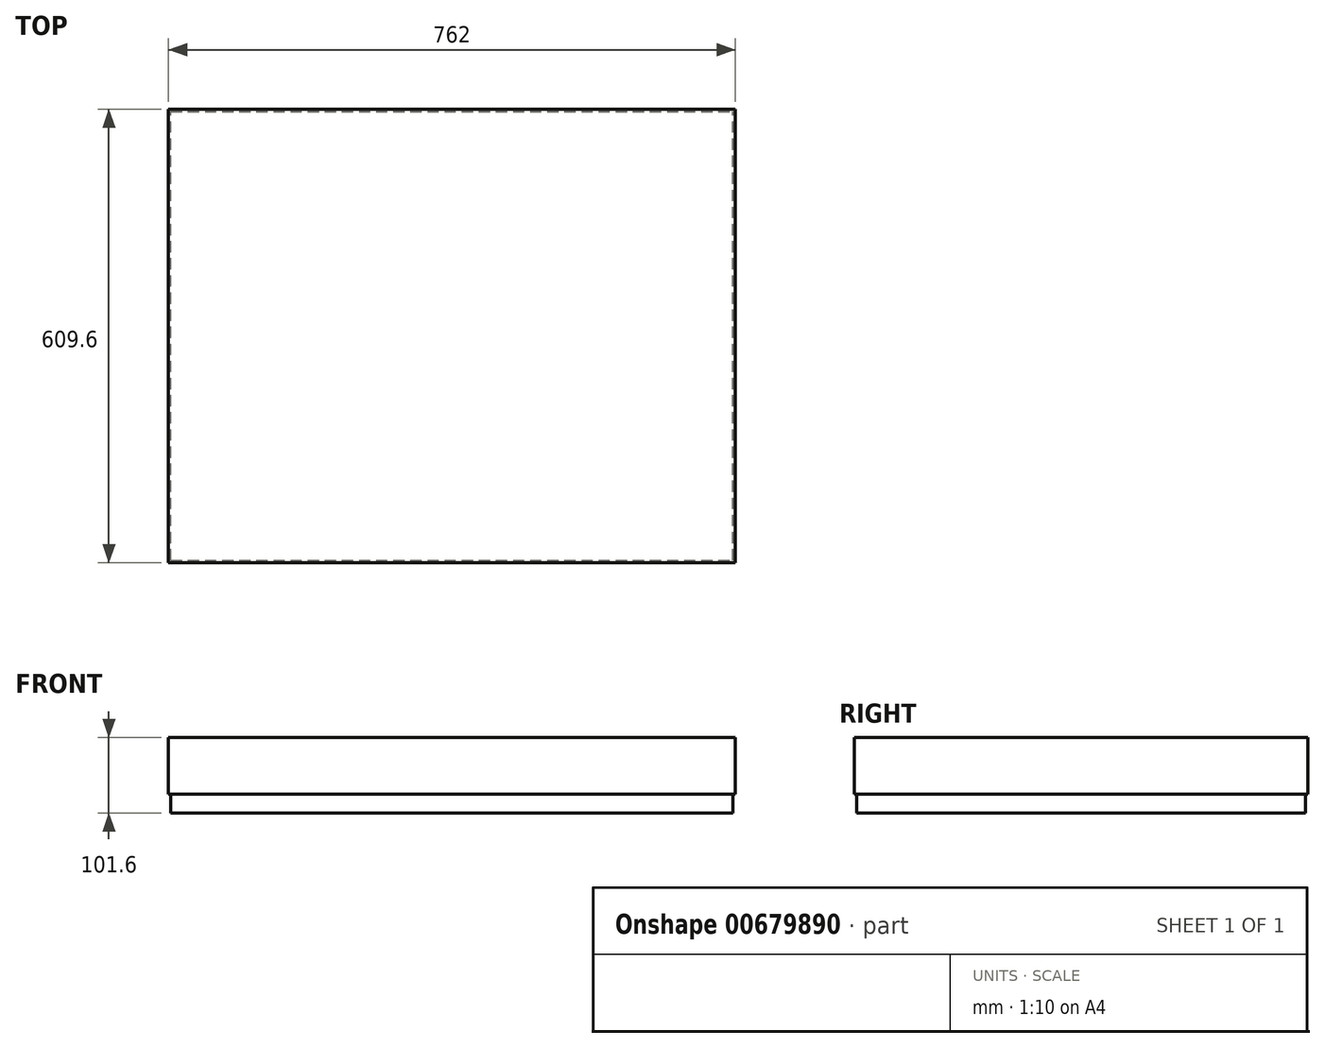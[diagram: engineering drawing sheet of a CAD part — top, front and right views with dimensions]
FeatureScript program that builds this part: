
annotation { "Feature Type Name" : "Feature", "Feature Type Description" : "" }
export const myFeature = defineFeature(function(context is Context, id is Id, definition is map)
    precondition{}
    {
        {
            var Q0;
            Q0=qCreatedBy(makeId("Top.planeOp"),FACE);
            var sketch = newSketch(context, id + "F0", { "sketchPlane" : qUnion([Q0])});
            skLineSegment(sketch, "E0.bottom", {"start": v(0, 0) * mm, "end": v(762, 0) * mm});
            skLineSegment(sketch, "E0.top", {"start": v(0, 609.6) * mm, "end": v(762, 609.6) * mm});
            skLineSegment(sketch, "E0.left", {"start": v(0, 0) * mm, "end": v(0, 609.6) * mm});
            skLineSegment(sketch, "E0.right", {"start": v(762, 0) * mm, "end": v(762, 609.6) * mm});
            skSolve(sketch);
        }
        {
            var Q0;
            Q0 = qSketchRegion(id + "F0", true);
            extrude(context, id + "F1", {"entities" : qUnion([Q0]), "depth" : 101.6 * mm, "offsetDistance" : 25.4 * mm});
        }
        {
            var Q0;
            Q0=makeQuery(id+"F1.opExtrude","CAP_FACE",FACE,{"disambiguationData":[OSD([sQuery(id+"F0.wireOp",EDGE,"E0.bottom"),sQuery(id+"F0.wireOp",EDGE,"E0.top"),sQuery(id+"F0.wireOp",EDGE,"E0.left"),sQuery(id+"F0.wireOp",EDGE,"E0.right")])],"isStart":true});
            var sketch = newSketch(context, id + "F2", { "sketchPlane" : qUnion([Q0])});
            skLineSegment(sketch, "E1.0", {"start": v(0, 0) * mm, "end": v(762, 0) * mm});
            skLineSegment(sketch, "E2.0", {"start": v(0, -609.6) * mm, "end": v(762, -609.6) * mm});
            skLineSegment(sketch, "E3.0", {"start": v(3.17, -3.18) * mm, "end": v(758.83, -3.18) * mm});
            skLineSegment(sketch, "E4.0", {"start": v(3.17, -606.43) * mm, "end": v(758.83, -606.43) * mm});
            skLineSegment(sketch, "E5", {"start": v(0, -606.43) * mm, "end": v(0, -609.6) * mm});
            skLineSegment(sketch, "E6", {"start": v(762, -606.43) * mm, "end": v(762, -609.6) * mm});
            skLineSegment(sketch, "E7", {"start": v(0, 0) * mm, "end": v(0, -3.18) * mm});
            skLineSegment(sketch, "E8", {"start": v(762, 0) * mm, "end": v(762, -3.18) * mm});
            skLineSegment(sketch, "E9.0", {"start": v(762, 0) * mm, "end": v(762, -609.6) * mm});
            skLineSegment(sketch, "E10.0", {"start": v(0, 0) * mm, "end": v(0, -609.6) * mm});
            skLineSegment(sketch, "E11.0", {"start": v(3.18, -3.17) * mm, "end": v(3.18, -606.43) * mm});
            skLineSegment(sketch, "E12.0", {"start": v(758.83, -3.17) * mm, "end": v(758.83, -606.43) * mm});
            skSolve(sketch);
        }
        {
            var Q0;
            Q0 = qSketchRegion(id + "F2", true);
            extrude(context, id + "F3", {"entities" : qUnion([Q0]), "operationType" : NewBodyOperationType.REMOVE, "oppositeDirection" : true, "depth" : 25.4 * mm, "offsetDistance" : 25.4 * mm});
        }
    });
